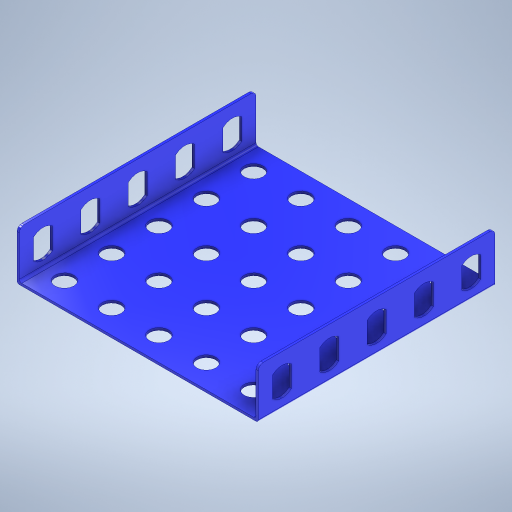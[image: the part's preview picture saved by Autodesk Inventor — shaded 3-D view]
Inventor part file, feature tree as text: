
AUTODESK INVENTOR PART (.ipt)
format: ipt  version: 2024 (Build 280153000, 153)  size: 384,000 bytes
history: native  units: mm
features: extrude x3, sketch x3, other x2, pattern_linear x2, fillet x2
ambient origin geometry x8: Origin, YZ Plane, XZ Plane, XY Plane, X Axis, Y Axis, Z Axis, Center Point
bodies: Body1 (feature_tree)
feature tree (12):
  other  "Těleso1"
  extrude  "Vysunutí1"  Depth=51.0mm
  extrude  "Vysunutí2"  Depth=25.5mm
  pattern_linear  "Obdélníkové pole1"  Spacing1=0.5mm  [1 undecoded]
  other  "Pracovní rovina1"
  extrude  "Vysunutí3"  Depth=0.5mm
  pattern_linear  "Obdélníkové pole2"  Spacing1=0.5mm  [1 undecoded]
  fillet  "Zaoblení1"  Radius=50.0mm
  fillet  "Zaoblení2"  Radius=10.0mm
  sketch  "Náčrt1"
  sketch  "Náčrt2"
  sketch  "Náčrt4"
note: 2 required parameter values undecoded (feature->parameter linkage not recoverable at this tier; creation-order binding heuristic only, values carry confidence <= 0.55)
